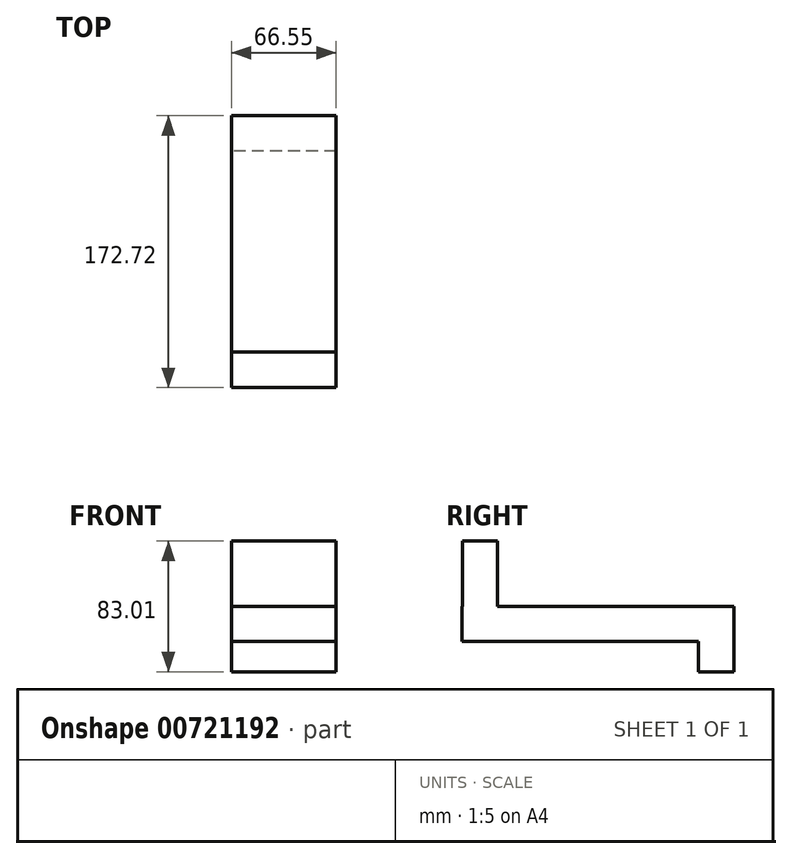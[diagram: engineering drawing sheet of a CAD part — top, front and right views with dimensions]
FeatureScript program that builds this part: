
annotation { "Feature Type Name" : "Feature", "Feature Type Description" : "" }
export const myFeature = defineFeature(function(context is Context, id is Id, definition is map)
    precondition{}
    {
        {
            var Q0;
            Q0=qCreatedBy(makeId("Right.planeOp"),FACE);
            var sketch = newSketch(context, id + "F0", { "sketchPlane" : qUnion([Q0])});
            skLineSegment(sketch, "E0.bottom", {"start": v(-86.36, 11.18) * mm, "end": v(86.36, 11.18) * mm});
            skLineSegment(sketch, "E0.top", {"start": v(-86.36, -11.18) * mm, "end": v(86.36, -11.18) * mm});
            skLineSegment(sketch, "E0.left", {"start": v(-86.36, 11.18) * mm, "end": v(-86.36, -11.18) * mm});
            skLineSegment(sketch, "E0.right", {"start": v(86.36, 11.18) * mm, "end": v(86.36, -11.18) * mm});
            skPoint(sketch, "E0.middle", {"position": v(0, 0) * mm});
            skSolve(sketch);
        }
        {
            var Q0;
            Q0=qCreatedBy(makeId("Right.planeOp"),FACE);
            var sketch = newSketch(context, id + "F1", { "sketchPlane" : qUnion([Q0])});
            skLineSegment(sketch, "E1.bottom", {"start": v(63.86, 10.82) * mm, "end": v(86.2, 10.82) * mm});
            skLineSegment(sketch, "E1.top", {"start": v(63.86, -30.33) * mm, "end": v(86.2, -30.33) * mm});
            skLineSegment(sketch, "E1.left", {"start": v(63.86, 10.82) * mm, "end": v(63.86, -30.33) * mm});
            skLineSegment(sketch, "E1.right", {"start": v(86.2, 10.82) * mm, "end": v(86.2, -30.33) * mm});
            skSolve(sketch);
        }
        {
            var Q0;
            Q0=qCreatedBy(makeId("Right.planeOp"),FACE);
            var sketch = newSketch(context, id + "F2", { "sketchPlane" : qUnion([Q0])});
            skLineSegment(sketch, "E2.bottom", {"start": v(-86.14, -10.82) * mm, "end": v(-63.79, -10.82) * mm});
            skLineSegment(sketch, "E2.top", {"start": v(-86.14, 52.68) * mm, "end": v(-63.79, 52.68) * mm});
            skLineSegment(sketch, "E2.left", {"start": v(-86.14, -10.82) * mm, "end": v(-86.14, 52.68) * mm});
            skLineSegment(sketch, "E2.right", {"start": v(-63.79, -10.82) * mm, "end": v(-63.79, 52.68) * mm});
            skSolve(sketch);
        }
        {
            var Q0;
            Q0=makeQuery(id+"F2.imprint","IMPRINT",FACE,{"disambiguationData":[TD([[makeQuery(id+"F2.imprint","IMPRINT",EDGE,{"derivedFrom":sQuery(id+"F2.wireOp",EDGE,"E2.bottom")}),1.0]])]});
            extrude(context, id + "F3", {"entities" : qUnion([Q0]), "oppositeDirection" : true, "depth" : 66.55 * mm, "offsetDistance" : 25.4 * mm});
        }
        {
            var Q0;
            Q0=makeQuery(id+"F0.imprint","IMPRINT",FACE,{"disambiguationData":[TD([[makeQuery(id+"F0.imprint","IMPRINT",EDGE,{"derivedFrom":sQuery(id+"F0.wireOp",EDGE,"E0.bottom")}),-1.0]])]});
            extrude(context, id + "F4", {"entities" : qUnion([Q0]), "operationType" : NewBodyOperationType.ADD, "oppositeDirection" : true, "depth" : 66.55 * mm, "offsetDistance" : 25.4 * mm});
        }
        {
            var Q0;
            Q0=makeQuery(id+"F1.imprint","IMPRINT",FACE,{"disambiguationData":[TD([[makeQuery(id+"F1.imprint","IMPRINT",EDGE,{"derivedFrom":sQuery(id+"F1.wireOp",EDGE,"E1.bottom")}),-1.0]])]});
            extrude(context, id + "F5", {"entities" : qUnion([Q0]), "operationType" : NewBodyOperationType.ADD, "oppositeDirection" : true, "depth" : 66.55 * mm, "offsetDistance" : 25.4 * mm});
        }
    });
